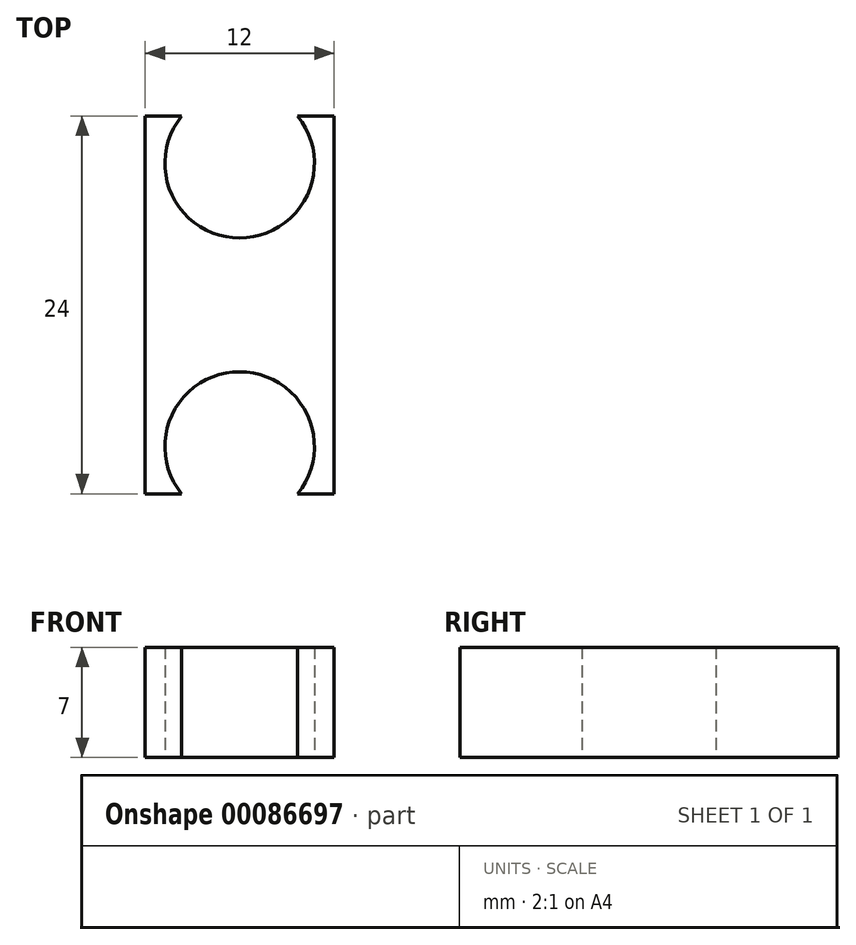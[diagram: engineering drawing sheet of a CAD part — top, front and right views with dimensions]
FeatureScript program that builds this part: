
annotation { "Feature Type Name" : "Feature", "Feature Type Description" : "" }
export const myFeature = defineFeature(function(context is Context, id is Id, definition is map)
    precondition{}
    {
        {
            var Q0;
            Q0=qCreatedBy(makeId("Top.planeOp"),FACE);
            var sketch = newSketch(context, id + "F0", { "sketchPlane" : qUnion([Q0])});
            skLineSegment(sketch, "E0.bottom", {"start": v(6, 12) * mm, "end": v(-6, 12) * mm});
            skLineSegment(sketch, "E0.top", {"start": v(6, -12) * mm, "end": v(-6, -12) * mm});
            skLineSegment(sketch, "E0.left", {"start": v(6, 12) * mm, "end": v(6, -12) * mm});
            skLineSegment(sketch, "E0.right", {"start": v(-6, 12) * mm, "end": v(-6, -12) * mm});
            skPoint(sketch, "E0.middle", {"position": v(0, 0) * mm});
            skCircle(sketch, "E1", {"center": v(0, 9) * mm, "radius": 4.75 * mm});
            skLineSegment(sketch, "E2", {"start": v(-15.84, 0) * mm, "end": v(20.57, 0) * mm, "construction": true});
            skPoint(sketch, "E2.endSnap0", {"position": v(6, 0) * mm});
            skCircle(sketch, "E3", {"center": v(0, -9) * mm, "radius": 4.75 * mm});
            skSolve(sketch);
        }
        {
            var Q0;
            {var subQ4=sQuery(id+"F0.wireOp",EDGE,"E0.left");Q0=makeQuery(id+"F0.imprint","IMPRINT",FACE,{"disambiguationData":[TD([[makeQuery(id+"F0.imprint","IMPRINT",EDGE,{"derivedFrom":subQ4}),-1.0]])]});}
            extrude(context, id + "F1", {"entities" : qUnion([Q0]), "depth" : 7 * mm});
        }
    });
